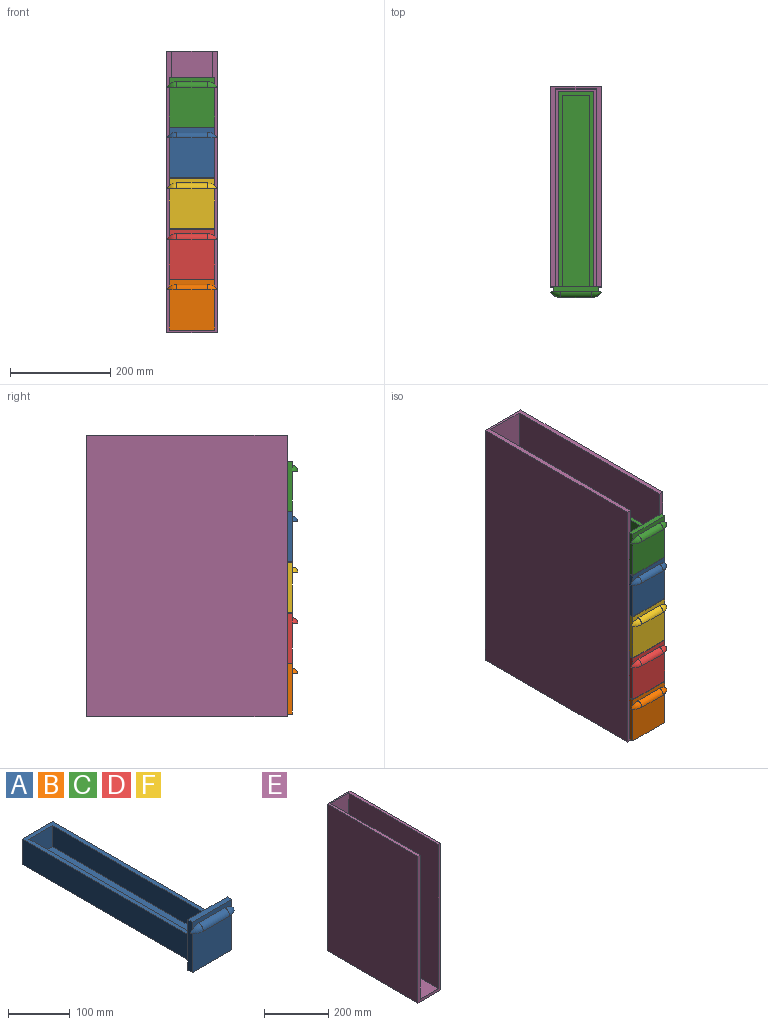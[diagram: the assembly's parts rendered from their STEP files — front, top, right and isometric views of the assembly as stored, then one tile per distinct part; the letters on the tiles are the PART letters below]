
ASSEMBLY  parts=6 mates=5
PART A: 27 faces, bbox 100x411x100 mm
  f0: plane 90x88mm, normal (0,-1,0), area 7860.2mm2, adj f8,f9,f11,f19,f20,f21
  f1: plane 90x14.36mm, normal (0,-1,0), area 860.9mm2, adj f8,f9,f10,f22,f23,f24
  f2: plane 390x50mm, normal (-1,0,0), area 19500mm2, adj f4,f5,f6,f7
  f3: plane 390x50mm, normal (1,0,0), area 19500mm2, adj f4,f5,f6,f7
  f4: plane 70x50mm, normal (0,1,0), area 3500mm2, adj f2,f3,f5,f6
  f5: plane 390x70mm, normal (0,0,1), area 6672mm2, adj f2,f3,f4,f7,f13,f14,f15
  f6: plane 390x70mm, normal (0,0,-1), area 27300mm2, adj f2,f3,f4,f7
  f7: plane 100x90mm, normal (0,1,0), area 5500mm2, adj f2,f3,f5,f6,f8,f9,f10,f11
  f8: plane 100x10mm, normal (-1,0,0), area 1000mm2, adj f0,f1,f7,f10,f11,f25
  f9: plane 100x10mm, normal (1,0,0), area 1000mm2, adj f0,f1,f7,f10,f11,f18
  f10: plane 90x10mm, normal (0,0,1), area 900mm2, adj f1,f7,f8,f9
  f11: plane 90x10mm, normal (0,0,-1), area 900mm2, adj f0,f7,f8,f9
  f12: plane 54x42mm, normal (0,1,0), area 2268mm2, adj f13,f14,f16,f17
  f13: plane 384x42mm, normal (1,0,0), area 16128mm2, adj f5,f12,f15,f16,f17
  f14: plane 384x42mm, normal (-1,0,0), area 16128mm2, adj f5,f12,f15,f16,f17
  f15: plane 54x42mm, normal (0,-1,0), area 2268mm2, adj f5,f13,f14,f17
  f16: plane 54x2mm, normal (0,0,-1), area 108mm2, adj f7,f12,f13,f14
  f17: plane 384x54mm, normal (0,0,1), area 20736mm2, adj f12,f13,f14,f15
  f18: plane 5.66x5.01mm, normal (0,1,0), area 14.6mm2, adj f9,f19,f24,f26
  f19: revolved ~16.34x8.22mm, area 155.5mm2, adj f0,f18,f20,f26
  f20: cylinder r=8mm len=60mm, axis (1,0,0), area 754mm2, adj f0,f19,f21,f26
  f21: revolved ~16.34x8.22mm, area 155.5mm2, adj f0,f20,f25,f26
  f22: revolved ~20x11mm, area 269.5mm2, adj f1,f23,f25,f26
  f23: cylinder r=11mm len=60mm, axis (1,0,0), area 1036.7mm2, adj f1,f22,f24,f26
  f24: revolved ~20x11mm, area 269.5mm2, adj f1,f18,f23,f26
  f25: plane 5.66x5.01mm, normal (0,1,0), area 14.6mm2, adj f8,f21,f22,f26
  f26: plane 100x11mm, normal (0,0,-1), area 308mm2, adj f18,f19,f20,f21,f22,f23,f24,f25
PART B: same geometry as A
PART C: same geometry as A
PART D: same geometry as A
PART E: 10 faces, bbox 100x400x560 mm
  f0: plane 560x100mm, normal (0,1,0), area 56000mm2, adj f1,f3,f4,f5
  f1: plane 560x400mm, normal (-1,0,0), area 224000mm2, adj f0,f2,f4,f5
  f2: plane 560x100mm, normal (0,-1,0), area 12000mm2, adj f1,f3,f4,f5,f7,f8,f9
  f3: plane 560x400mm, normal (1,0,0), area 224000mm2, adj f0,f2,f4,f5
  f4: plane 400x100mm, normal (0,0,1), area 8400mm2, adj f0,f1,f2,f3,f6,f7,f8
  f5: plane 400x100mm, normal (0,0,-1), area 40000mm2, adj f0,f1,f2,f3
  f6: plane 550x80mm, normal (0,-1,0), area 44000mm2, adj f4,f7,f8,f9
  f7: plane 550x395mm, normal (1,0,0), area 217250mm2, adj f2,f4,f6,f9
  f8: plane 550x395mm, normal (-1,0,0), area 217250mm2, adj f2,f4,f6,f9
  f9: plane 395x80mm, normal (0,0,1), area 31600mm2, adj f2,f6,f7,f8
PART F: same geometry as A
PLACE A t=(0,0,303)mm
PLACE B at identity
PLACE C t=(0,0,404)mm
PLACE D t=(0,0,101)mm
PLACE E at identity fixed
PLACE F t=(0,0,202)mm
MATE slider A.f7 <-> E.f2  axis (0,-1,0) through (0,-400,353)mm
MATE slider F.f7 <-> E.f2  axis (0,-1,0) through (0,-400,252)mm
MATE slider C.f7 <-> E.f2  axis (0,-1,0) through (0,-400,454)mm
MATE slider B.f7 <-> E.f2  axis (0,-1,0) through (0,-400,50)mm
MATE slider D.f7 <-> E.f2  axis (0,-1,0) through (0,-400,151)mm
